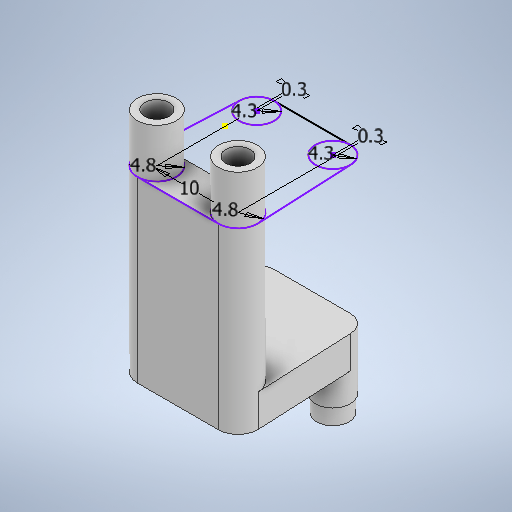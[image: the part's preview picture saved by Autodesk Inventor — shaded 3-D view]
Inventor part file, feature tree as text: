
AUTODESK INVENTOR PART (.ipt)
format: ipt  version: 2025.2 (Build 292293000, 293)  size: 710,144 bytes
history: native  units: in
note: dims shown in document units (in); Inventor stores cm internally (conversion verified against a paired STEP export)
features: projected_geometry x17, sketch x8, extrude x7
ambient origin geometry x8: Origin, YZ Plane, XZ Plane, XY Plane, X Axis, Y Axis, Z Axis, Center Point
bodies: Solid1 (feature_tree)
feature tree (32):
  sketch  "Sketch1"  dims[d0=0.189in d1=0.1693in d3=0.189in d5=0.1693in d7=0.2362in d8=0.0in]
  extrude  "Extrusion1"  Depth=0.2362in TaperAngle=0.0deg
  sketch  "Sketch2"  dims[d9=0.7087in d10=0.0in d11=0.1575in d12=0.0in]
  extrude  "Extrusion2"  Depth=0.1575in TaperAngle=0.0deg
  extrude  "Extrusion3"  Depth=0.1575in
  extrude  "Extrusion4"  Depth=0.0787in TaperAngle=0.0deg
  extrude  "Extrusion5"  Depth=0.1181in
  extrude  "Extrusion6"  Depth=0.3937in
  extrude  "Extrusion7"  Depth=0.0118in
  projected_geometry  "Projected Loop1"
  projected_geometry  "Projected Loop2"
  sketch  "Sketch3"  dims[d13=0.1378in d14=0.0in d15=0.1575in]
  projected_geometry  "Projected Loop3"
  projected_geometry  "Projected Loop4"
  projected_geometry  "Projected Loop5"
  projected_geometry  "Projected Loop6"
  projected_geometry  "Projected Loop7"
  projected_geometry  "Projected Loop8"
  projected_geometry  "Projected Loop9"
  sketch  "Sketch4"  dims[d16=0.1575in d17=0.0787in d18=0.0in]
  projected_geometry  "Projected Loop10"
  projected_geometry  "Projected Loop11"
  projected_geometry  "Projected Loop12"
  projected_geometry  "Projected Loop13"
  projected_geometry  "Projected Loop14"
  projected_geometry  "Projected Loop15"
  projected_geometry  "Projected Loop16"
  projected_geometry  "Projected Loop17"
  sketch  "Sketch5"  dims[d19=0.1181in d20=0.1181in]
  sketch  "Sketch6"  dims[d21=0.2362in d22=0.0in d24=0.3937in]
  sketch  "Sketch7"  dims[d25=0.0118in d26=0.0118in]
  sketch  "Sketch8"  dims[d27=0.1181in d28=0.1181in d29=0.3937in d30=0.0in]
